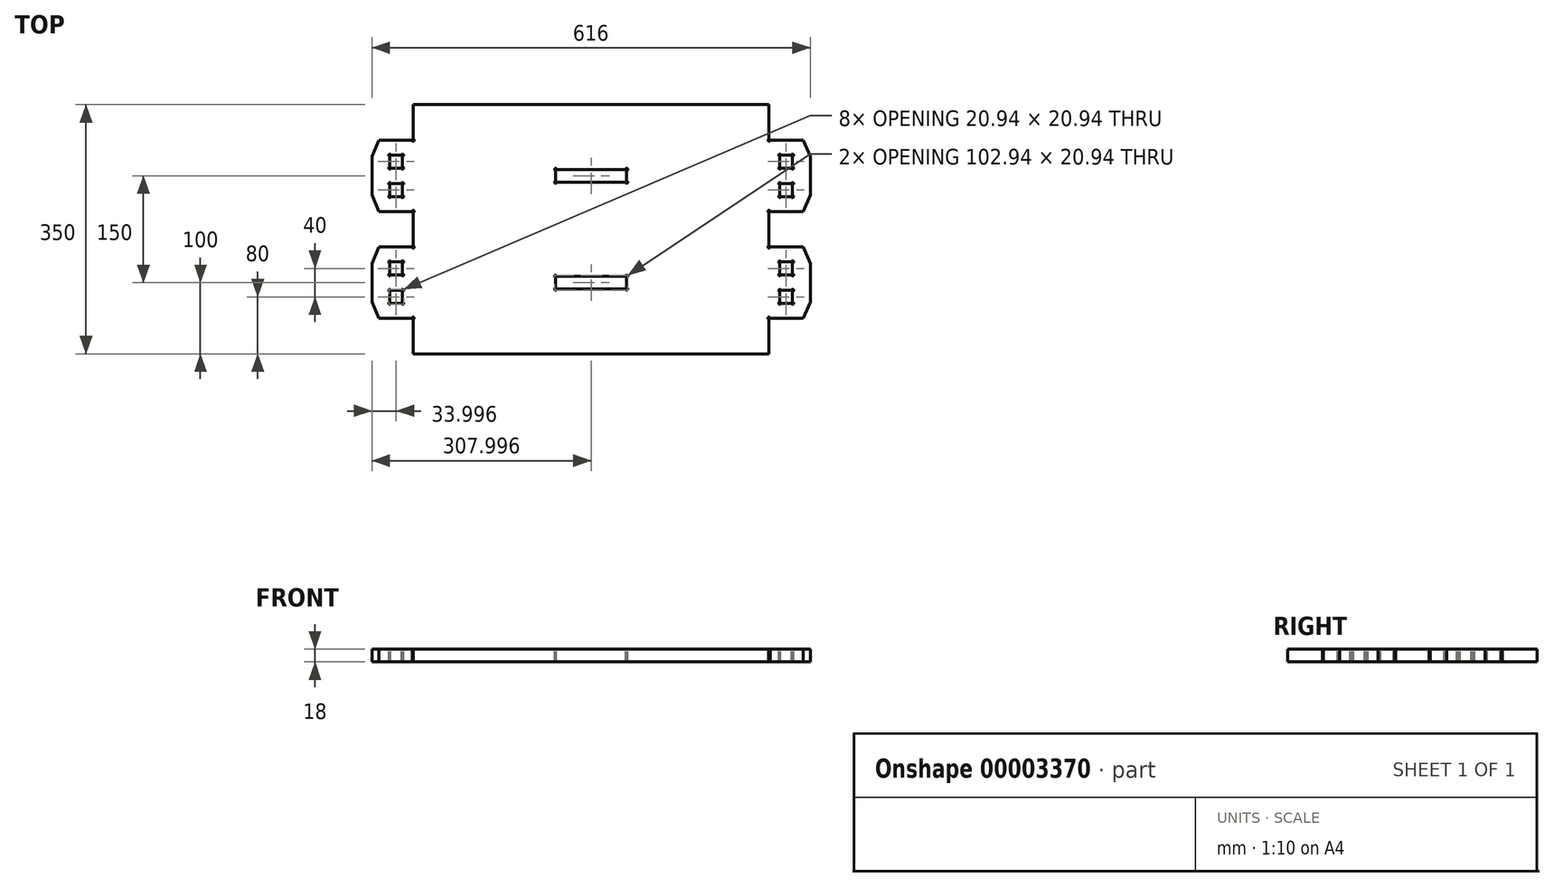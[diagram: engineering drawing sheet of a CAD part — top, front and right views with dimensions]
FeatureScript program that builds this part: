
annotation { "Feature Type Name" : "Feature", "Feature Type Description" : "" }
export const myFeature = defineFeature(function(context is Context, id is Id, definition is map)
    precondition{}
    {
        {
            var Q0;
            Q0=qCreatedBy(makeId("Top.planeOp"),FACE);
            var sketch = newSketch(context, id + "F0", { "sketchPlane" : qUnion([Q0])});
            skLineSegment(sketch, "E0.bottom", {"start": v(-333.81, 50) * mm, "end": v(166.19, 50) * mm});
            skLineSegment(sketch, "E0.top", {"start": v(-333.81, -300) * mm, "end": v(166.19, -300) * mm});
            skLineSegment(sketch, "E1.bottom", {"start": v(-333.81, -250) * mm, "end": v(-391.81, -250) * mm});
            skLineSegment(sketch, "E1.top", {"start": v(-333.81, -150) * mm, "end": v(-391.81, -150) * mm});
            skLineSegment(sketch, "E1.right", {"start": v(-391.81, -250) * mm, "end": v(-391.81, -150) * mm});
            skLineSegment(sketch, "E2.bottom", {"start": v(-333.81, -100) * mm, "end": v(-391.81, -100) * mm});
            skLineSegment(sketch, "E2.top", {"start": v(-333.81, 0) * mm, "end": v(-391.81, 0) * mm});
            skLineSegment(sketch, "E2.right", {"start": v(-391.81, -100) * mm, "end": v(-391.81, 0) * mm});
            skLineSegment(sketch, "E3.bottom", {"start": v(166.19, -250) * mm, "end": v(224.19, -250) * mm});
            skLineSegment(sketch, "E3.top", {"start": v(166.19, -150) * mm, "end": v(224.19, -150) * mm});
            skLineSegment(sketch, "E3.right", {"start": v(224.19, -250) * mm, "end": v(224.19, -150) * mm});
            skLineSegment(sketch, "E4.bottom", {"start": v(166.19, -100) * mm, "end": v(224.19, -100) * mm});
            skLineSegment(sketch, "E4.top", {"start": v(166.19, 0) * mm, "end": v(224.19, 0) * mm});
            skLineSegment(sketch, "E4.right", {"start": v(224.19, -100) * mm, "end": v(224.19, 0) * mm});
            skLineSegment(sketch, "E5", {"start": v(-333.81, -300) * mm, "end": v(-333.81, -250) * mm});
            skLineSegment(sketch, "E6", {"start": v(-333.81, -150) * mm, "end": v(-333.81, -100) * mm});
            skLineSegment(sketch, "E7", {"start": v(-333.81, 0) * mm, "end": v(-333.81, 50) * mm});
            skLineSegment(sketch, "E8", {"start": v(166.19, -300) * mm, "end": v(166.19, -250) * mm});
            skLineSegment(sketch, "E9", {"start": v(166.19, -150) * mm, "end": v(166.19, -100) * mm});
            skLineSegment(sketch, "E10", {"start": v(166.19, 0) * mm, "end": v(166.19, 50) * mm});
            skLineSegment(sketch, "E11", {"start": v(-366.81, -79) * mm, "end": v(-348.81, -79) * mm, "construction": true});
            skLineSegment(sketch, "E12", {"start": v(-366.81, -21) * mm, "end": v(-348.81, -21) * mm, "construction": true});
            skLineSegment(sketch, "E13.bottom", {"start": v(-348.81, -229) * mm, "end": v(-366.81, -229) * mm});
            skLineSegment(sketch, "E13.top", {"start": v(-348.81, -211) * mm, "end": v(-366.81, -211) * mm});
            skLineSegment(sketch, "E13.left", {"start": v(-348.81, -229) * mm, "end": v(-348.81, -211) * mm});
            skLineSegment(sketch, "E13.right", {"start": v(-366.81, -229) * mm, "end": v(-366.81, -211) * mm});
            skLineSegment(sketch, "E14.bottom", {"start": v(-348.81, -171) * mm, "end": v(-366.81, -171) * mm});
            skLineSegment(sketch, "E14.top", {"start": v(-348.81, -189) * mm, "end": v(-366.81, -189) * mm});
            skLineSegment(sketch, "E14.left", {"start": v(-348.81, -171) * mm, "end": v(-348.81, -189) * mm});
            skLineSegment(sketch, "E14.right", {"start": v(-366.81, -171) * mm, "end": v(-366.81, -189) * mm});
            skLineSegment(sketch, "E15.bottom", {"start": v(-348.81, -79) * mm, "end": v(-366.81, -79) * mm});
            skLineSegment(sketch, "E15.top", {"start": v(-348.81, -61) * mm, "end": v(-366.81, -61) * mm});
            skLineSegment(sketch, "E15.left", {"start": v(-348.81, -79) * mm, "end": v(-348.81, -61) * mm});
            skLineSegment(sketch, "E15.right", {"start": v(-366.81, -79) * mm, "end": v(-366.81, -61) * mm});
            skLineSegment(sketch, "E16.bottom", {"start": v(-348.81, -21) * mm, "end": v(-366.81, -21) * mm});
            skLineSegment(sketch, "E16.top", {"start": v(-348.81, -39) * mm, "end": v(-366.81, -39) * mm});
            skLineSegment(sketch, "E16.left", {"start": v(-348.81, -21) * mm, "end": v(-348.81, -39) * mm});
            skLineSegment(sketch, "E16.right", {"start": v(-366.81, -21) * mm, "end": v(-366.81, -39) * mm});
            skLineSegment(sketch, "E17.bottom", {"start": v(181.19, -229) * mm, "end": v(199.19, -229) * mm});
            skLineSegment(sketch, "E17.top", {"start": v(181.19, -211) * mm, "end": v(199.19, -211) * mm});
            skLineSegment(sketch, "E17.left", {"start": v(181.19, -229) * mm, "end": v(181.19, -211) * mm});
            skLineSegment(sketch, "E17.right", {"start": v(199.19, -229) * mm, "end": v(199.19, -211) * mm});
            skLineSegment(sketch, "E18.bottom", {"start": v(181.19, -171) * mm, "end": v(199.19, -171) * mm});
            skLineSegment(sketch, "E18.top", {"start": v(181.19, -189) * mm, "end": v(199.19, -189) * mm});
            skLineSegment(sketch, "E18.left", {"start": v(181.19, -171) * mm, "end": v(181.19, -189) * mm});
            skLineSegment(sketch, "E18.right", {"start": v(199.19, -171) * mm, "end": v(199.19, -189) * mm});
            skLineSegment(sketch, "E19.bottom", {"start": v(181.19, -79) * mm, "end": v(199.19, -79) * mm});
            skLineSegment(sketch, "E19.top", {"start": v(181.19, -61) * mm, "end": v(199.19, -61) * mm});
            skLineSegment(sketch, "E19.left", {"start": v(181.19, -79) * mm, "end": v(181.19, -61) * mm});
            skLineSegment(sketch, "E19.right", {"start": v(199.19, -79) * mm, "end": v(199.19, -61) * mm});
            skLineSegment(sketch, "E20.bottom", {"start": v(181.19, -21) * mm, "end": v(199.19, -21) * mm});
            skLineSegment(sketch, "E20.top", {"start": v(181.19, -39) * mm, "end": v(199.19, -39) * mm});
            skLineSegment(sketch, "E20.left", {"start": v(181.19, -21) * mm, "end": v(181.19, -39) * mm});
            skLineSegment(sketch, "E20.right", {"start": v(199.19, -21) * mm, "end": v(199.19, -39) * mm});
            skLineSegment(sketch, "E21.bottom", {"start": v(-133.81, -209) * mm, "end": v(-33.81, -209) * mm});
            skLineSegment(sketch, "E21.top", {"start": v(-133.81, -191) * mm, "end": v(-33.81, -191) * mm});
            skLineSegment(sketch, "E21.left", {"start": v(-133.81, -209) * mm, "end": v(-133.81, -191) * mm});
            skLineSegment(sketch, "E21.right", {"start": v(-33.81, -209) * mm, "end": v(-33.81, -191) * mm});
            skLineSegment(sketch, "E22.bottom", {"start": v(-133.81, -59) * mm, "end": v(-33.81, -59) * mm});
            skLineSegment(sketch, "E22.top", {"start": v(-133.81, -41) * mm, "end": v(-33.81, -41) * mm});
            skLineSegment(sketch, "E22.left", {"start": v(-133.81, -59) * mm, "end": v(-133.81, -41) * mm});
            skLineSegment(sketch, "E22.right", {"start": v(-33.81, -59) * mm, "end": v(-33.81, -41) * mm});
            skSolve(sketch);
        }
        {
            var Q0;
            Q0=makeQuery(id+"F0.imprint","IMPRINT",FACE,{"disambiguationData":[TD([[makeQuery(id+"F0.imprint","IMPRINT",EDGE,{"derivedFrom":sQuery(id+"F0.wireOp",EDGE,"E0.bottom")}),-1.0]])]});
            extrude(context, id + "F1", {"entities" : qUnion([Q0]), "depth" : 18 * mm});
        }
        {
            var Q0;
            Q0=makeQuery(id+"F1.opExtrude","SWEPT_EDGE",EDGE,{"disambiguationData":[OSD([sQuery(id+"F0.wireOp",EDGE,"E1.bottom"),sQuery(id+"F0.wireOp",EDGE,"E1.right")])]});
            var Q1;
            Q1=makeQuery(id+"F1.opExtrude","SWEPT_EDGE",EDGE,{"disambiguationData":[OSD([sQuery(id+"F0.wireOp",EDGE,"E1.top"),sQuery(id+"F0.wireOp",EDGE,"E1.right")])]});
            var Q2;
            Q2=makeQuery(id+"F1.opExtrude","SWEPT_EDGE",EDGE,{"disambiguationData":[OSD([sQuery(id+"F0.wireOp",EDGE,"E2.bottom"),sQuery(id+"F0.wireOp",EDGE,"E2.right")])]});
            var Q3;
            Q3=makeQuery(id+"F1.opExtrude","SWEPT_EDGE",EDGE,{"disambiguationData":[OSD([sQuery(id+"F0.wireOp",EDGE,"E3.top"),sQuery(id+"F0.wireOp",EDGE,"E3.right")])]});
            var Q4;
            Q4=makeQuery(id+"F1.opExtrude","SWEPT_EDGE",EDGE,{"disambiguationData":[OSD([sQuery(id+"F0.wireOp",EDGE,"E4.top"),sQuery(id+"F0.wireOp",EDGE,"E4.right")])]});
            chamfer(context, id + "F2", {"entities" : qUnion([Q0, Q1, Q2, Q3, Q4]), "chamferType" : ChamferType.TWO_OFFSETS, "width1" : 10 * mm, "oppositeDirection" : false, "width2" : 23 * mm, "tangentPropagation" : true});
        }
        {
            var Q0;
            Q0=makeQuery(id+"F1.opExtrude","SWEPT_EDGE",EDGE,{"disambiguationData":[OSD([sQuery(id+"F0.wireOp",EDGE,"E2.top"),sQuery(id+"F0.wireOp",EDGE,"E2.right")])]});
            var Q1;
            Q1=makeQuery(id+"F1.opExtrude","SWEPT_EDGE",EDGE,{"disambiguationData":[OSD([sQuery(id+"F0.wireOp",EDGE,"E4.bottom"),sQuery(id+"F0.wireOp",EDGE,"E4.right")])]});
            var Q2;
            Q2=makeQuery(id+"F1.opExtrude","SWEPT_EDGE",EDGE,{"disambiguationData":[OSD([sQuery(id+"F0.wireOp",EDGE,"E3.bottom"),sQuery(id+"F0.wireOp",EDGE,"E3.right")])]});
            chamfer(context, id + "F3", {"entities" : qUnion([Q0, Q1, Q2]), "chamferType" : ChamferType.TWO_OFFSETS, "width1" : 23 * mm, "oppositeDirection" : false, "width2" : 10 * mm, "tangentPropagation" : true});
        }
        {
            var Q0;
            Q0=makeQuery(id+"F1.opExtrude","CAP_FACE",FACE,{"disambiguationData":[OSD([sQuery(id+"F0.wireOp",EDGE,"E0.bottom"),sQuery(id+"F0.wireOp",EDGE,"E0.top"),sQuery(id+"F0.wireOp",EDGE,"E1.bottom"),sQuery(id+"F0.wireOp",EDGE,"E1.top"),sQuery(id+"F0.wireOp",EDGE,"E1.right"),sQuery(id+"F0.wireOp",EDGE,"E2.bottom"),sQuery(id+"F0.wireOp",EDGE,"E2.top"),sQuery(id+"F0.wireOp",EDGE,"E2.right"),sQuery(id+"F0.wireOp",EDGE,"E3.bottom"),sQuery(id+"F0.wireOp",EDGE,"E3.top"),sQuery(id+"F0.wireOp",EDGE,"E3.right"),sQuery(id+"F0.wireOp",EDGE,"E4.bottom"),sQuery(id+"F0.wireOp",EDGE,"E4.top"),sQuery(id+"F0.wireOp",EDGE,"E4.right"),sQuery(id+"F0.wireOp",EDGE,"E5"),sQuery(id+"F0.wireOp",EDGE,"E6"),sQuery(id+"F0.wireOp",EDGE,"E7"),sQuery(id+"F0.wireOp",EDGE,"E8"),sQuery(id+"F0.wireOp",EDGE,"E9"),sQuery(id+"F0.wireOp",EDGE,"E10"),sQuery(id+"F0.wireOp",EDGE,"E13.bottom"),sQuery(id+"F0.wireOp",EDGE,"E13.top"),sQuery(id+"F0.wireOp",EDGE,"E13.left"),sQuery(id+"F0.wireOp",EDGE,"E13.right"),sQuery(id+"F0.wireOp",EDGE,"E14.bottom"),sQuery(id+"F0.wireOp",EDGE,"E14.top"),sQuery(id+"F0.wireOp",EDGE,"E14.left"),sQuery(id+"F0.wireOp",EDGE,"E14.right"),sQuery(id+"F0.wireOp",EDGE,"E15.bottom"),sQuery(id+"F0.wireOp",EDGE,"E15.top"),sQuery(id+"F0.wireOp",EDGE,"E15.left"),sQuery(id+"F0.wireOp",EDGE,"E15.right"),sQuery(id+"F0.wireOp",EDGE,"E16.bottom"),sQuery(id+"F0.wireOp",EDGE,"E16.top"),sQuery(id+"F0.wireOp",EDGE,"E16.left"),sQuery(id+"F0.wireOp",EDGE,"E16.right"),sQuery(id+"F0.wireOp",EDGE,"E17.bottom"),sQuery(id+"F0.wireOp",EDGE,"E17.top"),sQuery(id+"F0.wireOp",EDGE,"E17.left"),sQuery(id+"F0.wireOp",EDGE,"E17.right"),sQuery(id+"F0.wireOp",EDGE,"E18.bottom"),sQuery(id+"F0.wireOp",EDGE,"E18.top"),sQuery(id+"F0.wireOp",EDGE,"E18.left"),sQuery(id+"F0.wireOp",EDGE,"E18.right"),sQuery(id+"F0.wireOp",EDGE,"E19.bottom"),sQuery(id+"F0.wireOp",EDGE,"E19.top"),sQuery(id+"F0.wireOp",EDGE,"E19.left"),sQuery(id+"F0.wireOp",EDGE,"E19.right"),sQuery(id+"F0.wireOp",EDGE,"E20.bottom"),sQuery(id+"F0.wireOp",EDGE,"E20.top"),sQuery(id+"F0.wireOp",EDGE,"E20.left"),sQuery(id+"F0.wireOp",EDGE,"E20.right"),sQuery(id+"F0.wireOp",EDGE,"E21.bottom"),sQuery(id+"F0.wireOp",EDGE,"E21.top"),sQuery(id+"F0.wireOp",EDGE,"E21.left"),sQuery(id+"F0.wireOp",EDGE,"E21.right"),sQuery(id+"F0.wireOp",EDGE,"E22.bottom"),sQuery(id+"F0.wireOp",EDGE,"E22.top"),sQuery(id+"F0.wireOp",EDGE,"E22.left"),sQuery(id+"F0.wireOp",EDGE,"E22.right")])],"isStart":false});
            var sketch = newSketch(context, id + "F4", { "sketchPlane" : qUnion([Q0])});
            skCircle(sketch, "E23", {"center": v(-348.81, -211) * mm, "radius": 1.5 * mm});
            skCircle(sketch, "E24", {"center": v(-348.81, -229) * mm, "radius": 1.5 * mm});
            skCircle(sketch, "E25", {"center": v(-366.81, -229) * mm, "radius": 1.5 * mm});
            skCircle(sketch, "E26", {"center": v(-366.81, -211) * mm, "radius": 1.5 * mm});
            skCircle(sketch, "E27", {"center": v(-366.81, -189) * mm, "radius": 1.5 * mm});
            skCircle(sketch, "E28", {"center": v(-366.81, -171) * mm, "radius": 1.5 * mm});
            skCircle(sketch, "E29", {"center": v(-348.81, -171) * mm, "radius": 1.5 * mm});
            skCircle(sketch, "E30", {"center": v(-348.81, -189) * mm, "radius": 1.5 * mm});
            skCircle(sketch, "E31", {"center": v(-348.81, -79) * mm, "radius": 1.5 * mm});
            skCircle(sketch, "E32", {"center": v(-348.81, -61) * mm, "radius": 1.5 * mm});
            skCircle(sketch, "E33", {"center": v(-366.81, -79) * mm, "radius": 1.5 * mm});
            skCircle(sketch, "E34", {"center": v(-366.81, -61) * mm, "radius": 1.5 * mm});
            skCircle(sketch, "E35", {"center": v(-348.81, -39) * mm, "radius": 1.5 * mm});
            skCircle(sketch, "E36", {"center": v(-348.81, -21) * mm, "radius": 1.5 * mm});
            skCircle(sketch, "E37", {"center": v(-366.81, -39) * mm, "radius": 1.5 * mm});
            skCircle(sketch, "E38", {"center": v(-366.81, -21) * mm, "radius": 1.5 * mm});
            skCircle(sketch, "E39", {"center": v(-133.81, -209) * mm, "radius": 1.5 * mm});
            skCircle(sketch, "E40", {"center": v(-133.81, -191) * mm, "radius": 1.5 * mm});
            skCircle(sketch, "E41", {"center": v(-33.81, -191) * mm, "radius": 1.5 * mm});
            skCircle(sketch, "E42", {"center": v(-33.81, -209) * mm, "radius": 1.5 * mm});
            skCircle(sketch, "E43", {"center": v(-133.81, -59) * mm, "radius": 1.5 * mm});
            skCircle(sketch, "E44", {"center": v(-133.81, -41) * mm, "radius": 1.5 * mm});
            skCircle(sketch, "E45", {"center": v(-33.81, -41) * mm, "radius": 1.5 * mm});
            skCircle(sketch, "E46", {"center": v(-33.81, -59) * mm, "radius": 1.5 * mm});
            skCircle(sketch, "E47", {"center": v(181.19, -229) * mm, "radius": 1.5 * mm});
            skCircle(sketch, "E48", {"center": v(181.19, -211) * mm, "radius": 1.5 * mm});
            skCircle(sketch, "E49", {"center": v(199.19, -211) * mm, "radius": 1.5 * mm});
            skCircle(sketch, "E50", {"center": v(199.19, -229) * mm, "radius": 1.5 * mm});
            skCircle(sketch, "E51", {"center": v(199.19, -171) * mm, "radius": 1.5 * mm});
            skCircle(sketch, "E52", {"center": v(181.19, -171) * mm, "radius": 1.5 * mm});
            skCircle(sketch, "E53", {"center": v(181.19, -189) * mm, "radius": 1.5 * mm});
            skCircle(sketch, "E54", {"center": v(181.19, -79) * mm, "radius": 1.5 * mm});
            skCircle(sketch, "E55", {"center": v(181.19, -61) * mm, "radius": 1.5 * mm});
            skCircle(sketch, "E56", {"center": v(199.19, -61) * mm, "radius": 1.5 * mm});
            skCircle(sketch, "E57", {"center": v(199.19, -79) * mm, "radius": 1.5 * mm});
            skCircle(sketch, "E58", {"center": v(199.19, -39) * mm, "radius": 1.5 * mm});
            skCircle(sketch, "E59", {"center": v(181.19, -39) * mm, "radius": 1.5 * mm});
            skCircle(sketch, "E60", {"center": v(181.19, -21) * mm, "radius": 1.5 * mm});
            skCircle(sketch, "E61", {"center": v(199.19, -21) * mm, "radius": 1.5 * mm});
            skCircle(sketch, "E62", {"center": v(166.19, -100) * mm, "radius": 1.5 * mm});
            skCircle(sketch, "E63", {"center": v(166.19, -150) * mm, "radius": 1.5 * mm});
            skCircle(sketch, "E64", {"center": v(166.19, -250) * mm, "radius": 1.5 * mm});
            skCircle(sketch, "E65", {"center": v(166.19, 0) * mm, "radius": 1.5 * mm});
            skCircle(sketch, "E66", {"center": v(-333.81, -250) * mm, "radius": 1.5 * mm});
            skCircle(sketch, "E67", {"center": v(-333.81, -150) * mm, "radius": 1.5 * mm});
            skCircle(sketch, "E68", {"center": v(-333.81, -100) * mm, "radius": 1.5 * mm});
            skCircle(sketch, "E69", {"center": v(-333.81, 0) * mm, "radius": 1.5 * mm});
            skCircle(sketch, "E70", {"center": v(199.19, -189) * mm, "radius": 1.5 * mm});
            skSolve(sketch);
        }
        {
            var Q0;
            {var subQ1=sQuery(id+"F4.wireOp",EDGE,"E62");var subQ3=makeQuery(id+"F1.opExtrude","CAP_EDGE",EDGE,{"disambiguationData":[OSD([sQuery(id+"F0.wireOp",EDGE,"E9")])],"isStart":false});var subQ6=makeQuery(id+"F4.imprint","INTERSECT",VERTEX,{"derivedFrom":[subQ3,subQ1]});var subQ9=sQuery(id+"F4.wireOp",EDGE,"E63");var subQ13=makeQuery(id+"F4.imprint","INTERSECT",VERTEX,{"derivedFrom":[subQ3,subQ9]});var subQ16=sQuery(id+"F4.wireOp",EDGE,"E64");var subQ18=makeQuery(id+"F1.opExtrude","CAP_EDGE",EDGE,{"disambiguationData":[OSD([sQuery(id+"F0.wireOp",EDGE,"E8")])],"isStart":false});var subQ21=makeQuery(id+"F4.imprint","INTERSECT",VERTEX,{"derivedFrom":[subQ18,subQ16]});var subQ24=sQuery(id+"F4.wireOp",EDGE,"E65");var subQ26=makeQuery(id+"F1.opExtrude","CAP_EDGE",EDGE,{"disambiguationData":[OSD([sQuery(id+"F0.wireOp",EDGE,"E10")])],"isStart":false});var subQ29=makeQuery(id+"F4.imprint","INTERSECT",VERTEX,{"derivedFrom":[subQ26,subQ24]});var subQ32=sQuery(id+"F4.wireOp",EDGE,"E66");var subQ34=makeQuery(id+"F1.opExtrude","CAP_EDGE",EDGE,{"disambiguationData":[OSD([sQuery(id+"F0.wireOp",EDGE,"E5")])],"isStart":false});var subQ37=makeQuery(id+"F4.imprint","INTERSECT",VERTEX,{"derivedFrom":[subQ34,subQ32]});var subQ40=sQuery(id+"F4.wireOp",EDGE,"E67");var subQ42=makeQuery(id+"F1.opExtrude","CAP_EDGE",EDGE,{"disambiguationData":[OSD([sQuery(id+"F0.wireOp",EDGE,"E6")])],"isStart":false});var subQ45=makeQuery(id+"F4.imprint","INTERSECT",VERTEX,{"derivedFrom":[subQ42,subQ40]});var subQ48=sQuery(id+"F4.wireOp",EDGE,"E68");var subQ52=makeQuery(id+"F4.imprint","INTERSECT",VERTEX,{"derivedFrom":[subQ42,subQ48]});var subQ55=sQuery(id+"F4.wireOp",EDGE,"E69");var subQ57=makeQuery(id+"F1.opExtrude","CAP_EDGE",EDGE,{"disambiguationData":[OSD([sQuery(id+"F0.wireOp",EDGE,"E7")])],"isStart":false});var subQ60=makeQuery(id+"F4.imprint","INTERSECT",VERTEX,{"derivedFrom":[subQ57,subQ55]});var subQ63=sQuery(id+"F4.wireOp",EDGE,"E23");var subQ65=makeQuery(id+"F1.opExtrude","CAP_EDGE",EDGE,{"disambiguationData":[OSD([sQuery(id+"F0.wireOp",EDGE,"E13.top")])],"isStart":false});var subQ68=makeQuery(id+"F4.imprint","INTERSECT",VERTEX,{"derivedFrom":[subQ65,subQ63]});var subQ70=sQuery(id+"F4.wireOp",EDGE,"E24");var subQ72=makeQuery(id+"F1.opExtrude","CAP_EDGE",EDGE,{"disambiguationData":[OSD([sQuery(id+"F0.wireOp",EDGE,"E13.bottom")])],"isStart":false});var subQ75=makeQuery(id+"F4.imprint","INTERSECT",VERTEX,{"derivedFrom":[subQ72,subQ70]});var subQ78=sQuery(id+"F4.wireOp",EDGE,"E25");var subQ82=makeQuery(id+"F4.imprint","INTERSECT",VERTEX,{"derivedFrom":[subQ72,subQ78]});var subQ84=sQuery(id+"F4.wireOp",EDGE,"E26");var subQ88=makeQuery(id+"F4.imprint","INTERSECT",VERTEX,{"derivedFrom":[subQ65,subQ84]});var subQ91=sQuery(id+"F4.wireOp",EDGE,"E27");var subQ93=makeQuery(id+"F1.opExtrude","CAP_EDGE",EDGE,{"disambiguationData":[OSD([sQuery(id+"F0.wireOp",EDGE,"E14.top")])],"isStart":false});var subQ96=makeQuery(id+"F4.imprint","INTERSECT",VERTEX,{"derivedFrom":[subQ93,subQ91]});var subQ98=sQuery(id+"F4.wireOp",EDGE,"E28");var subQ100=makeQuery(id+"F1.opExtrude","CAP_EDGE",EDGE,{"disambiguationData":[OSD([sQuery(id+"F0.wireOp",EDGE,"E14.bottom")])],"isStart":false});var subQ103=makeQuery(id+"F4.imprint","INTERSECT",VERTEX,{"derivedFrom":[subQ100,subQ98]});var subQ106=sQuery(id+"F4.wireOp",EDGE,"E29");var subQ110=makeQuery(id+"F4.imprint","INTERSECT",VERTEX,{"derivedFrom":[subQ100,subQ106]});var subQ112=sQuery(id+"F4.wireOp",EDGE,"E30");var subQ116=makeQuery(id+"F4.imprint","INTERSECT",VERTEX,{"derivedFrom":[subQ93,subQ112]});var subQ119=sQuery(id+"F4.wireOp",EDGE,"E31");var subQ121=makeQuery(id+"F1.opExtrude","CAP_EDGE",EDGE,{"disambiguationData":[OSD([sQuery(id+"F0.wireOp",EDGE,"E15.bottom")])],"isStart":false});var subQ124=makeQuery(id+"F4.imprint","INTERSECT",VERTEX,{"derivedFrom":[subQ121,subQ119]});var subQ126=sQuery(id+"F4.wireOp",EDGE,"E32");var subQ128=makeQuery(id+"F1.opExtrude","CAP_EDGE",EDGE,{"disambiguationData":[OSD([sQuery(id+"F0.wireOp",EDGE,"E15.top")])],"isStart":false});var subQ131=makeQuery(id+"F4.imprint","INTERSECT",VERTEX,{"derivedFrom":[subQ128,subQ126]});var subQ134=sQuery(id+"F4.wireOp",EDGE,"E33");var subQ138=makeQuery(id+"F4.imprint","INTERSECT",VERTEX,{"derivedFrom":[subQ121,subQ134]});var subQ140=sQuery(id+"F4.wireOp",EDGE,"E34");var subQ144=makeQuery(id+"F4.imprint","INTERSECT",VERTEX,{"derivedFrom":[subQ128,subQ140]});var subQ147=sQuery(id+"F4.wireOp",EDGE,"E35");var subQ149=makeQuery(id+"F1.opExtrude","CAP_EDGE",EDGE,{"disambiguationData":[OSD([sQuery(id+"F0.wireOp",EDGE,"E16.top")])],"isStart":false});var subQ152=makeQuery(id+"F4.imprint","INTERSECT",VERTEX,{"derivedFrom":[subQ149,subQ147]});var subQ154=sQuery(id+"F4.wireOp",EDGE,"E36");var subQ156=makeQuery(id+"F1.opExtrude","CAP_EDGE",EDGE,{"disambiguationData":[OSD([sQuery(id+"F0.wireOp",EDGE,"E16.bottom")])],"isStart":false});var subQ159=makeQuery(id+"F4.imprint","INTERSECT",VERTEX,{"derivedFrom":[subQ156,subQ154]});var subQ162=sQuery(id+"F4.wireOp",EDGE,"E37");var subQ166=makeQuery(id+"F4.imprint","INTERSECT",VERTEX,{"derivedFrom":[subQ149,subQ162]});var subQ168=sQuery(id+"F4.wireOp",EDGE,"E38");var subQ172=makeQuery(id+"F4.imprint","INTERSECT",VERTEX,{"derivedFrom":[subQ156,subQ168]});var subQ175=sQuery(id+"F4.wireOp",EDGE,"E39");var subQ177=makeQuery(id+"F1.opExtrude","CAP_EDGE",EDGE,{"disambiguationData":[OSD([sQuery(id+"F0.wireOp",EDGE,"E21.bottom")])],"isStart":false});var subQ180=makeQuery(id+"F4.imprint","INTERSECT",VERTEX,{"derivedFrom":[subQ177,subQ175]});var subQ182=sQuery(id+"F4.wireOp",EDGE,"E40");var subQ184=makeQuery(id+"F1.opExtrude","CAP_EDGE",EDGE,{"disambiguationData":[OSD([sQuery(id+"F0.wireOp",EDGE,"E21.top")])],"isStart":false});var subQ187=makeQuery(id+"F4.imprint","INTERSECT",VERTEX,{"derivedFrom":[subQ184,subQ182]});var subQ190=sQuery(id+"F4.wireOp",EDGE,"E41");var subQ194=makeQuery(id+"F4.imprint","INTERSECT",VERTEX,{"derivedFrom":[subQ184,subQ190]});var subQ196=sQuery(id+"F4.wireOp",EDGE,"E42");var subQ200=makeQuery(id+"F4.imprint","INTERSECT",VERTEX,{"derivedFrom":[subQ177,subQ196]});var subQ203=sQuery(id+"F4.wireOp",EDGE,"E43");var subQ205=makeQuery(id+"F1.opExtrude","CAP_EDGE",EDGE,{"disambiguationData":[OSD([sQuery(id+"F0.wireOp",EDGE,"E22.bottom")])],"isStart":false});var subQ208=makeQuery(id+"F4.imprint","INTERSECT",VERTEX,{"derivedFrom":[subQ205,subQ203]});var subQ210=sQuery(id+"F4.wireOp",EDGE,"E44");var subQ212=makeQuery(id+"F1.opExtrude","CAP_EDGE",EDGE,{"disambiguationData":[OSD([sQuery(id+"F0.wireOp",EDGE,"E22.top")])],"isStart":false});var subQ215=makeQuery(id+"F4.imprint","INTERSECT",VERTEX,{"derivedFrom":[subQ212,subQ210]});var subQ218=sQuery(id+"F4.wireOp",EDGE,"E45");var subQ222=makeQuery(id+"F4.imprint","INTERSECT",VERTEX,{"derivedFrom":[subQ212,subQ218]});var subQ224=sQuery(id+"F4.wireOp",EDGE,"E46");var subQ228=makeQuery(id+"F4.imprint","INTERSECT",VERTEX,{"derivedFrom":[subQ205,subQ224]});var subQ231=sQuery(id+"F4.wireOp",EDGE,"E47");var subQ233=makeQuery(id+"F1.opExtrude","CAP_EDGE",EDGE,{"disambiguationData":[OSD([sQuery(id+"F0.wireOp",EDGE,"E17.bottom")])],"isStart":false});var subQ236=makeQuery(id+"F4.imprint","INTERSECT",VERTEX,{"derivedFrom":[subQ233,subQ231]});var subQ238=sQuery(id+"F4.wireOp",EDGE,"E48");var subQ240=makeQuery(id+"F1.opExtrude","CAP_EDGE",EDGE,{"disambiguationData":[OSD([sQuery(id+"F0.wireOp",EDGE,"E17.top")])],"isStart":false});var subQ243=makeQuery(id+"F4.imprint","INTERSECT",VERTEX,{"derivedFrom":[subQ240,subQ238]});var subQ246=sQuery(id+"F4.wireOp",EDGE,"E49");var subQ250=makeQuery(id+"F4.imprint","INTERSECT",VERTEX,{"derivedFrom":[subQ240,subQ246]});var subQ252=sQuery(id+"F4.wireOp",EDGE,"E50");var subQ256=makeQuery(id+"F4.imprint","INTERSECT",VERTEX,{"derivedFrom":[subQ233,subQ252]});var subQ259=sQuery(id+"F4.wireOp",EDGE,"E51");var subQ261=makeQuery(id+"F1.opExtrude","CAP_EDGE",EDGE,{"disambiguationData":[OSD([sQuery(id+"F0.wireOp",EDGE,"E18.bottom")])],"isStart":false});var subQ264=makeQuery(id+"F4.imprint","INTERSECT",VERTEX,{"derivedFrom":[subQ261,subQ259]});var subQ267=sQuery(id+"F4.wireOp",EDGE,"E52");var subQ271=makeQuery(id+"F4.imprint","INTERSECT",VERTEX,{"derivedFrom":[subQ261,subQ267]});var subQ273=sQuery(id+"F4.wireOp",EDGE,"E53");var subQ275=makeQuery(id+"F1.opExtrude","CAP_EDGE",EDGE,{"disambiguationData":[OSD([sQuery(id+"F0.wireOp",EDGE,"E18.top")])],"isStart":false});var subQ278=makeQuery(id+"F4.imprint","INTERSECT",VERTEX,{"derivedFrom":[subQ275,subQ273]});var subQ281=sQuery(id+"F4.wireOp",EDGE,"E54");var subQ283=makeQuery(id+"F1.opExtrude","CAP_EDGE",EDGE,{"disambiguationData":[OSD([sQuery(id+"F0.wireOp",EDGE,"E19.bottom")])],"isStart":false});var subQ286=makeQuery(id+"F4.imprint","INTERSECT",VERTEX,{"derivedFrom":[subQ283,subQ281]});var subQ288=sQuery(id+"F4.wireOp",EDGE,"E55");var subQ290=makeQuery(id+"F1.opExtrude","CAP_EDGE",EDGE,{"disambiguationData":[OSD([sQuery(id+"F0.wireOp",EDGE,"E19.top")])],"isStart":false});var subQ293=makeQuery(id+"F4.imprint","INTERSECT",VERTEX,{"derivedFrom":[subQ290,subQ288]});var subQ296=sQuery(id+"F4.wireOp",EDGE,"E56");var subQ300=makeQuery(id+"F4.imprint","INTERSECT",VERTEX,{"derivedFrom":[subQ290,subQ296]});var subQ302=sQuery(id+"F4.wireOp",EDGE,"E57");var subQ306=makeQuery(id+"F4.imprint","INTERSECT",VERTEX,{"derivedFrom":[subQ283,subQ302]});var subQ309=sQuery(id+"F4.wireOp",EDGE,"E58");var subQ311=makeQuery(id+"F1.opExtrude","CAP_EDGE",EDGE,{"disambiguationData":[OSD([sQuery(id+"F0.wireOp",EDGE,"E20.top")])],"isStart":false});var subQ314=makeQuery(id+"F4.imprint","INTERSECT",VERTEX,{"derivedFrom":[subQ311,subQ309]});var subQ317=sQuery(id+"F4.wireOp",EDGE,"E59");var subQ321=makeQuery(id+"F4.imprint","INTERSECT",VERTEX,{"derivedFrom":[subQ311,subQ317]});var subQ323=sQuery(id+"F4.wireOp",EDGE,"E60");var subQ325=makeQuery(id+"F1.opExtrude","CAP_EDGE",EDGE,{"disambiguationData":[OSD([sQuery(id+"F0.wireOp",EDGE,"E20.bottom")])],"isStart":false});var subQ328=makeQuery(id+"F4.imprint","INTERSECT",VERTEX,{"derivedFrom":[subQ325,subQ323]});var subQ330=sQuery(id+"F4.wireOp",EDGE,"E61");var subQ334=makeQuery(id+"F4.imprint","INTERSECT",VERTEX,{"derivedFrom":[subQ325,subQ330]});var subQ336=sQuery(id+"F4.wireOp",EDGE,"E70");var subQ340=makeQuery(id+"F4.imprint","INTERSECT",VERTEX,{"derivedFrom":[subQ275,subQ336]});Q0=qUnion([makeQuery(id+"F4.imprint","IMPRINT",FACE,{"disambiguationData":[TD([[makeQuery(id+"F4.imprint","IMPRINT",EDGE,{"disambiguationData":[TD([[subQ6,-1.0]])],"derivedFrom":subQ1}),1.0]])]}),makeQuery(id+"F4.imprint","IMPRINT",FACE,{"disambiguationData":[TD([[makeQuery(id+"F4.imprint","IMPRINT",EDGE,{"disambiguationData":[TD([[subQ13,1.0]])],"derivedFrom":subQ9}),1.0]])]}),makeQuery(id+"F4.imprint","IMPRINT",FACE,{"disambiguationData":[TD([[makeQuery(id+"F4.imprint","IMPRINT",EDGE,{"disambiguationData":[TD([[subQ21,-1.0]])],"derivedFrom":subQ16}),1.0]])]}),makeQuery(id+"F4.imprint","IMPRINT",FACE,{"disambiguationData":[TD([[makeQuery(id+"F4.imprint","IMPRINT",EDGE,{"disambiguationData":[TD([[subQ29,1.0]])],"derivedFrom":subQ24}),1.0]])]}),makeQuery(id+"F4.imprint","IMPRINT",FACE,{"disambiguationData":[TD([[makeQuery(id+"F4.imprint","IMPRINT",EDGE,{"disambiguationData":[TD([[subQ37,1.0]])],"derivedFrom":subQ32}),1.0]])]}),makeQuery(id+"F4.imprint","IMPRINT",FACE,{"disambiguationData":[TD([[makeQuery(id+"F4.imprint","IMPRINT",EDGE,{"disambiguationData":[TD([[subQ45,-1.0]])],"derivedFrom":subQ40}),1.0]])]}),makeQuery(id+"F4.imprint","IMPRINT",FACE,{"disambiguationData":[TD([[makeQuery(id+"F4.imprint","IMPRINT",EDGE,{"disambiguationData":[TD([[subQ52,1.0]])],"derivedFrom":subQ48}),1.0]])]}),makeQuery(id+"F4.imprint","IMPRINT",FACE,{"disambiguationData":[TD([[makeQuery(id+"F4.imprint","IMPRINT",EDGE,{"disambiguationData":[TD([[subQ60,-1.0]])],"derivedFrom":subQ55}),1.0]])]}),makeQuery(id+"F4.imprint","IMPRINT",FACE,{"disambiguationData":[TD([[makeQuery(id+"F4.imprint","IMPRINT",EDGE,{"disambiguationData":[TD([[subQ68,-1.0]])],"derivedFrom":subQ63}),1.0]])]}),makeQuery(id+"F4.imprint","IMPRINT",FACE,{"disambiguationData":[TD([[makeQuery(id+"F4.imprint","IMPRINT",EDGE,{"disambiguationData":[TD([[subQ68,1.0]])],"derivedFrom":subQ63}),1.0]])]}),makeQuery(id+"F4.imprint","IMPRINT",FACE,{"disambiguationData":[TD([[makeQuery(id+"F4.imprint","IMPRINT",EDGE,{"disambiguationData":[TD([[subQ75,1.0]])],"derivedFrom":subQ70}),1.0]])]}),makeQuery(id+"F4.imprint","IMPRINT",FACE,{"disambiguationData":[TD([[makeQuery(id+"F4.imprint","IMPRINT",EDGE,{"disambiguationData":[TD([[subQ75,-1.0]])],"derivedFrom":subQ70}),1.0]])]}),makeQuery(id+"F4.imprint","IMPRINT",FACE,{"disambiguationData":[TD([[makeQuery(id+"F4.imprint","IMPRINT",EDGE,{"disambiguationData":[TD([[subQ82,-1.0]])],"derivedFrom":subQ78}),1.0]])]}),makeQuery(id+"F4.imprint","IMPRINT",FACE,{"disambiguationData":[TD([[makeQuery(id+"F4.imprint","IMPRINT",EDGE,{"disambiguationData":[TD([[subQ82,1.0]])],"derivedFrom":subQ78}),1.0]])]}),makeQuery(id+"F4.imprint","IMPRINT",FACE,{"disambiguationData":[TD([[makeQuery(id+"F4.imprint","IMPRINT",EDGE,{"disambiguationData":[TD([[subQ88,-1.0]])],"derivedFrom":subQ84}),1.0]])]}),makeQuery(id+"F4.imprint","IMPRINT",FACE,{"disambiguationData":[TD([[makeQuery(id+"F4.imprint","IMPRINT",EDGE,{"disambiguationData":[TD([[subQ88,1.0]])],"derivedFrom":subQ84}),1.0]])]}),makeQuery(id+"F4.imprint","IMPRINT",FACE,{"disambiguationData":[TD([[makeQuery(id+"F4.imprint","IMPRINT",EDGE,{"disambiguationData":[TD([[subQ96,-1.0]])],"derivedFrom":subQ91}),1.0]])]}),makeQuery(id+"F4.imprint","IMPRINT",FACE,{"disambiguationData":[TD([[makeQuery(id+"F4.imprint","IMPRINT",EDGE,{"disambiguationData":[TD([[subQ96,1.0]])],"derivedFrom":subQ91}),1.0]])]}),makeQuery(id+"F4.imprint","IMPRINT",FACE,{"disambiguationData":[TD([[makeQuery(id+"F4.imprint","IMPRINT",EDGE,{"disambiguationData":[TD([[subQ103,-1.0]])],"derivedFrom":subQ98}),1.0]])]}),makeQuery(id+"F4.imprint","IMPRINT",FACE,{"disambiguationData":[TD([[makeQuery(id+"F4.imprint","IMPRINT",EDGE,{"disambiguationData":[TD([[subQ103,1.0]])],"derivedFrom":subQ98}),1.0]])]}),makeQuery(id+"F4.imprint","IMPRINT",FACE,{"disambiguationData":[TD([[makeQuery(id+"F4.imprint","IMPRINT",EDGE,{"disambiguationData":[TD([[subQ110,-1.0]])],"derivedFrom":subQ106}),1.0]])]}),makeQuery(id+"F4.imprint","IMPRINT",FACE,{"disambiguationData":[TD([[makeQuery(id+"F4.imprint","IMPRINT",EDGE,{"disambiguationData":[TD([[subQ110,1.0]])],"derivedFrom":subQ106}),1.0]])]}),makeQuery(id+"F4.imprint","IMPRINT",FACE,{"disambiguationData":[TD([[makeQuery(id+"F4.imprint","IMPRINT",EDGE,{"disambiguationData":[TD([[subQ116,1.0]])],"derivedFrom":subQ112}),1.0]])]}),makeQuery(id+"F4.imprint","IMPRINT",FACE,{"disambiguationData":[TD([[makeQuery(id+"F4.imprint","IMPRINT",EDGE,{"disambiguationData":[TD([[subQ116,-1.0]])],"derivedFrom":subQ112}),1.0]])]}),makeQuery(id+"F4.imprint","IMPRINT",FACE,{"disambiguationData":[TD([[makeQuery(id+"F4.imprint","IMPRINT",EDGE,{"disambiguationData":[TD([[subQ124,1.0]])],"derivedFrom":subQ119}),1.0]])]}),makeQuery(id+"F4.imprint","IMPRINT",FACE,{"disambiguationData":[TD([[makeQuery(id+"F4.imprint","IMPRINT",EDGE,{"disambiguationData":[TD([[subQ124,-1.0]])],"derivedFrom":subQ119}),1.0]])]}),makeQuery(id+"F4.imprint","IMPRINT",FACE,{"disambiguationData":[TD([[makeQuery(id+"F4.imprint","IMPRINT",EDGE,{"disambiguationData":[TD([[subQ131,-1.0]])],"derivedFrom":subQ126}),1.0]])]}),makeQuery(id+"F4.imprint","IMPRINT",FACE,{"disambiguationData":[TD([[makeQuery(id+"F4.imprint","IMPRINT",EDGE,{"disambiguationData":[TD([[subQ131,1.0]])],"derivedFrom":subQ126}),1.0]])]}),makeQuery(id+"F4.imprint","IMPRINT",FACE,{"disambiguationData":[TD([[makeQuery(id+"F4.imprint","IMPRINT",EDGE,{"disambiguationData":[TD([[subQ138,-1.0]])],"derivedFrom":subQ134}),1.0]])]}),makeQuery(id+"F4.imprint","IMPRINT",FACE,{"disambiguationData":[TD([[makeQuery(id+"F4.imprint","IMPRINT",EDGE,{"disambiguationData":[TD([[subQ138,1.0]])],"derivedFrom":subQ134}),1.0]])]}),makeQuery(id+"F4.imprint","IMPRINT",FACE,{"disambiguationData":[TD([[makeQuery(id+"F4.imprint","IMPRINT",EDGE,{"disambiguationData":[TD([[subQ144,-1.0]])],"derivedFrom":subQ140}),1.0]])]}),makeQuery(id+"F4.imprint","IMPRINT",FACE,{"disambiguationData":[TD([[makeQuery(id+"F4.imprint","IMPRINT",EDGE,{"disambiguationData":[TD([[subQ144,1.0]])],"derivedFrom":subQ140}),1.0]])]}),makeQuery(id+"F4.imprint","IMPRINT",FACE,{"disambiguationData":[TD([[makeQuery(id+"F4.imprint","IMPRINT",EDGE,{"disambiguationData":[TD([[subQ152,1.0]])],"derivedFrom":subQ147}),1.0]])]}),makeQuery(id+"F4.imprint","IMPRINT",FACE,{"disambiguationData":[TD([[makeQuery(id+"F4.imprint","IMPRINT",EDGE,{"disambiguationData":[TD([[subQ152,-1.0]])],"derivedFrom":subQ147}),1.0]])]}),makeQuery(id+"F4.imprint","IMPRINT",FACE,{"disambiguationData":[TD([[makeQuery(id+"F4.imprint","IMPRINT",EDGE,{"disambiguationData":[TD([[subQ159,-1.0]])],"derivedFrom":subQ154}),1.0]])]}),makeQuery(id+"F4.imprint","IMPRINT",FACE,{"disambiguationData":[TD([[makeQuery(id+"F4.imprint","IMPRINT",EDGE,{"disambiguationData":[TD([[subQ159,1.0]])],"derivedFrom":subQ154}),1.0]])]}),makeQuery(id+"F4.imprint","IMPRINT",FACE,{"disambiguationData":[TD([[makeQuery(id+"F4.imprint","IMPRINT",EDGE,{"disambiguationData":[TD([[subQ166,-1.0]])],"derivedFrom":subQ162}),1.0]])]}),makeQuery(id+"F4.imprint","IMPRINT",FACE,{"disambiguationData":[TD([[makeQuery(id+"F4.imprint","IMPRINT",EDGE,{"disambiguationData":[TD([[subQ166,1.0]])],"derivedFrom":subQ162}),1.0]])]}),makeQuery(id+"F4.imprint","IMPRINT",FACE,{"disambiguationData":[TD([[makeQuery(id+"F4.imprint","IMPRINT",EDGE,{"disambiguationData":[TD([[subQ172,-1.0]])],"derivedFrom":subQ168}),1.0]])]}),makeQuery(id+"F4.imprint","IMPRINT",FACE,{"disambiguationData":[TD([[makeQuery(id+"F4.imprint","IMPRINT",EDGE,{"disambiguationData":[TD([[subQ172,1.0]])],"derivedFrom":subQ168}),1.0]])]}),makeQuery(id+"F4.imprint","IMPRINT",FACE,{"disambiguationData":[TD([[makeQuery(id+"F4.imprint","IMPRINT",EDGE,{"disambiguationData":[TD([[subQ180,-1.0]])],"derivedFrom":subQ175}),1.0]])]}),makeQuery(id+"F4.imprint","IMPRINT",FACE,{"disambiguationData":[TD([[makeQuery(id+"F4.imprint","IMPRINT",EDGE,{"disambiguationData":[TD([[subQ180,1.0]])],"derivedFrom":subQ175}),1.0]])]}),makeQuery(id+"F4.imprint","IMPRINT",FACE,{"disambiguationData":[TD([[makeQuery(id+"F4.imprint","IMPRINT",EDGE,{"disambiguationData":[TD([[subQ187,-1.0]])],"derivedFrom":subQ182}),1.0]])]}),makeQuery(id+"F4.imprint","IMPRINT",FACE,{"disambiguationData":[TD([[makeQuery(id+"F4.imprint","IMPRINT",EDGE,{"disambiguationData":[TD([[subQ187,1.0]])],"derivedFrom":subQ182}),1.0]])]}),makeQuery(id+"F4.imprint","IMPRINT",FACE,{"disambiguationData":[TD([[makeQuery(id+"F4.imprint","IMPRINT",EDGE,{"disambiguationData":[TD([[subQ194,-1.0]])],"derivedFrom":subQ190}),1.0]])]}),makeQuery(id+"F4.imprint","IMPRINT",FACE,{"disambiguationData":[TD([[makeQuery(id+"F4.imprint","IMPRINT",EDGE,{"disambiguationData":[TD([[subQ194,1.0]])],"derivedFrom":subQ190}),1.0]])]}),makeQuery(id+"F4.imprint","IMPRINT",FACE,{"disambiguationData":[TD([[makeQuery(id+"F4.imprint","IMPRINT",EDGE,{"disambiguationData":[TD([[subQ200,1.0]])],"derivedFrom":subQ196}),1.0]])]}),makeQuery(id+"F4.imprint","IMPRINT",FACE,{"disambiguationData":[TD([[makeQuery(id+"F4.imprint","IMPRINT",EDGE,{"disambiguationData":[TD([[subQ200,-1.0]])],"derivedFrom":subQ196}),1.0]])]}),makeQuery(id+"F4.imprint","IMPRINT",FACE,{"disambiguationData":[TD([[makeQuery(id+"F4.imprint","IMPRINT",EDGE,{"disambiguationData":[TD([[subQ208,-1.0]])],"derivedFrom":subQ203}),1.0]])]}),makeQuery(id+"F4.imprint","IMPRINT",FACE,{"disambiguationData":[TD([[makeQuery(id+"F4.imprint","IMPRINT",EDGE,{"disambiguationData":[TD([[subQ208,1.0]])],"derivedFrom":subQ203}),1.0]])]}),makeQuery(id+"F4.imprint","IMPRINT",FACE,{"disambiguationData":[TD([[makeQuery(id+"F4.imprint","IMPRINT",EDGE,{"disambiguationData":[TD([[subQ215,-1.0]])],"derivedFrom":subQ210}),1.0]])]}),makeQuery(id+"F4.imprint","IMPRINT",FACE,{"disambiguationData":[TD([[makeQuery(id+"F4.imprint","IMPRINT",EDGE,{"disambiguationData":[TD([[subQ215,1.0]])],"derivedFrom":subQ210}),1.0]])]}),makeQuery(id+"F4.imprint","IMPRINT",FACE,{"disambiguationData":[TD([[makeQuery(id+"F4.imprint","IMPRINT",EDGE,{"disambiguationData":[TD([[subQ222,-1.0]])],"derivedFrom":subQ218}),1.0]])]}),makeQuery(id+"F4.imprint","IMPRINT",FACE,{"disambiguationData":[TD([[makeQuery(id+"F4.imprint","IMPRINT",EDGE,{"disambiguationData":[TD([[subQ222,1.0]])],"derivedFrom":subQ218}),1.0]])]}),makeQuery(id+"F4.imprint","IMPRINT",FACE,{"disambiguationData":[TD([[makeQuery(id+"F4.imprint","IMPRINT",EDGE,{"disambiguationData":[TD([[subQ228,1.0]])],"derivedFrom":subQ224}),1.0]])]}),makeQuery(id+"F4.imprint","IMPRINT",FACE,{"disambiguationData":[TD([[makeQuery(id+"F4.imprint","IMPRINT",EDGE,{"disambiguationData":[TD([[subQ228,-1.0]])],"derivedFrom":subQ224}),1.0]])]}),makeQuery(id+"F4.imprint","IMPRINT",FACE,{"disambiguationData":[TD([[makeQuery(id+"F4.imprint","IMPRINT",EDGE,{"disambiguationData":[TD([[subQ236,-1.0]])],"derivedFrom":subQ231}),1.0]])]}),makeQuery(id+"F4.imprint","IMPRINT",FACE,{"disambiguationData":[TD([[makeQuery(id+"F4.imprint","IMPRINT",EDGE,{"disambiguationData":[TD([[subQ236,1.0]])],"derivedFrom":subQ231}),1.0]])]}),makeQuery(id+"F4.imprint","IMPRINT",FACE,{"disambiguationData":[TD([[makeQuery(id+"F4.imprint","IMPRINT",EDGE,{"disambiguationData":[TD([[subQ243,-1.0]])],"derivedFrom":subQ238}),1.0]])]}),makeQuery(id+"F4.imprint","IMPRINT",FACE,{"disambiguationData":[TD([[makeQuery(id+"F4.imprint","IMPRINT",EDGE,{"disambiguationData":[TD([[subQ243,1.0]])],"derivedFrom":subQ238}),1.0]])]}),makeQuery(id+"F4.imprint","IMPRINT",FACE,{"disambiguationData":[TD([[makeQuery(id+"F4.imprint","IMPRINT",EDGE,{"disambiguationData":[TD([[subQ250,-1.0]])],"derivedFrom":subQ246}),1.0]])]}),makeQuery(id+"F4.imprint","IMPRINT",FACE,{"disambiguationData":[TD([[makeQuery(id+"F4.imprint","IMPRINT",EDGE,{"disambiguationData":[TD([[subQ250,1.0]])],"derivedFrom":subQ246}),1.0]])]}),makeQuery(id+"F4.imprint","IMPRINT",FACE,{"disambiguationData":[TD([[makeQuery(id+"F4.imprint","IMPRINT",EDGE,{"disambiguationData":[TD([[subQ256,1.0]])],"derivedFrom":subQ252}),1.0]])]}),makeQuery(id+"F4.imprint","IMPRINT",FACE,{"disambiguationData":[TD([[makeQuery(id+"F4.imprint","IMPRINT",EDGE,{"disambiguationData":[TD([[subQ256,-1.0]])],"derivedFrom":subQ252}),1.0]])]}),makeQuery(id+"F4.imprint","IMPRINT",FACE,{"disambiguationData":[TD([[makeQuery(id+"F4.imprint","IMPRINT",EDGE,{"disambiguationData":[TD([[subQ264,-1.0]])],"derivedFrom":subQ259}),1.0]])]}),makeQuery(id+"F4.imprint","IMPRINT",FACE,{"disambiguationData":[TD([[makeQuery(id+"F4.imprint","IMPRINT",EDGE,{"disambiguationData":[TD([[subQ264,1.0]])],"derivedFrom":subQ259}),1.0]])]}),makeQuery(id+"F4.imprint","IMPRINT",FACE,{"disambiguationData":[TD([[makeQuery(id+"F4.imprint","IMPRINT",EDGE,{"disambiguationData":[TD([[subQ271,-1.0]])],"derivedFrom":subQ267}),1.0]])]}),makeQuery(id+"F4.imprint","IMPRINT",FACE,{"disambiguationData":[TD([[makeQuery(id+"F4.imprint","IMPRINT",EDGE,{"disambiguationData":[TD([[subQ271,1.0]])],"derivedFrom":subQ267}),1.0]])]}),makeQuery(id+"F4.imprint","IMPRINT",FACE,{"disambiguationData":[TD([[makeQuery(id+"F4.imprint","IMPRINT",EDGE,{"disambiguationData":[TD([[subQ278,-1.0]])],"derivedFrom":subQ273}),1.0]])]}),makeQuery(id+"F4.imprint","IMPRINT",FACE,{"disambiguationData":[TD([[makeQuery(id+"F4.imprint","IMPRINT",EDGE,{"disambiguationData":[TD([[subQ278,1.0]])],"derivedFrom":subQ273}),1.0]])]}),makeQuery(id+"F4.imprint","IMPRINT",FACE,{"disambiguationData":[TD([[makeQuery(id+"F4.imprint","IMPRINT",EDGE,{"disambiguationData":[TD([[subQ286,-1.0]])],"derivedFrom":subQ281}),1.0]])]}),makeQuery(id+"F4.imprint","IMPRINT",FACE,{"disambiguationData":[TD([[makeQuery(id+"F4.imprint","IMPRINT",EDGE,{"disambiguationData":[TD([[subQ286,1.0]])],"derivedFrom":subQ281}),1.0]])]}),makeQuery(id+"F4.imprint","IMPRINT",FACE,{"disambiguationData":[TD([[makeQuery(id+"F4.imprint","IMPRINT",EDGE,{"disambiguationData":[TD([[subQ293,-1.0]])],"derivedFrom":subQ288}),1.0]])]}),makeQuery(id+"F4.imprint","IMPRINT",FACE,{"disambiguationData":[TD([[makeQuery(id+"F4.imprint","IMPRINT",EDGE,{"disambiguationData":[TD([[subQ293,1.0]])],"derivedFrom":subQ288}),1.0]])]}),makeQuery(id+"F4.imprint","IMPRINT",FACE,{"disambiguationData":[TD([[makeQuery(id+"F4.imprint","IMPRINT",EDGE,{"disambiguationData":[TD([[subQ300,-1.0]])],"derivedFrom":subQ296}),1.0]])]}),makeQuery(id+"F4.imprint","IMPRINT",FACE,{"disambiguationData":[TD([[makeQuery(id+"F4.imprint","IMPRINT",EDGE,{"disambiguationData":[TD([[subQ300,1.0]])],"derivedFrom":subQ296}),1.0]])]}),makeQuery(id+"F4.imprint","IMPRINT",FACE,{"disambiguationData":[TD([[makeQuery(id+"F4.imprint","IMPRINT",EDGE,{"disambiguationData":[TD([[subQ306,1.0]])],"derivedFrom":subQ302}),1.0]])]}),makeQuery(id+"F4.imprint","IMPRINT",FACE,{"disambiguationData":[TD([[makeQuery(id+"F4.imprint","IMPRINT",EDGE,{"disambiguationData":[TD([[subQ306,-1.0]])],"derivedFrom":subQ302}),1.0]])]}),makeQuery(id+"F4.imprint","IMPRINT",FACE,{"disambiguationData":[TD([[makeQuery(id+"F4.imprint","IMPRINT",EDGE,{"disambiguationData":[TD([[subQ314,1.0]])],"derivedFrom":subQ309}),1.0]])]}),makeQuery(id+"F4.imprint","IMPRINT",FACE,{"disambiguationData":[TD([[makeQuery(id+"F4.imprint","IMPRINT",EDGE,{"disambiguationData":[TD([[subQ314,-1.0]])],"derivedFrom":subQ309}),1.0]])]}),makeQuery(id+"F4.imprint","IMPRINT",FACE,{"disambiguationData":[TD([[makeQuery(id+"F4.imprint","IMPRINT",EDGE,{"disambiguationData":[TD([[subQ321,-1.0]])],"derivedFrom":subQ317}),1.0]])]}),makeQuery(id+"F4.imprint","IMPRINT",FACE,{"disambiguationData":[TD([[makeQuery(id+"F4.imprint","IMPRINT",EDGE,{"disambiguationData":[TD([[subQ321,1.0]])],"derivedFrom":subQ317}),1.0]])]}),makeQuery(id+"F4.imprint","IMPRINT",FACE,{"disambiguationData":[TD([[makeQuery(id+"F4.imprint","IMPRINT",EDGE,{"disambiguationData":[TD([[subQ328,-1.0]])],"derivedFrom":subQ323}),1.0]])]}),makeQuery(id+"F4.imprint","IMPRINT",FACE,{"disambiguationData":[TD([[makeQuery(id+"F4.imprint","IMPRINT",EDGE,{"disambiguationData":[TD([[subQ328,1.0]])],"derivedFrom":subQ323}),1.0]])]}),makeQuery(id+"F4.imprint","IMPRINT",FACE,{"disambiguationData":[TD([[makeQuery(id+"F4.imprint","IMPRINT",EDGE,{"disambiguationData":[TD([[subQ334,-1.0]])],"derivedFrom":subQ330}),1.0]])]}),makeQuery(id+"F4.imprint","IMPRINT",FACE,{"disambiguationData":[TD([[makeQuery(id+"F4.imprint","IMPRINT",EDGE,{"disambiguationData":[TD([[subQ334,1.0]])],"derivedFrom":subQ330}),1.0]])]}),makeQuery(id+"F4.imprint","IMPRINT",FACE,{"disambiguationData":[TD([[makeQuery(id+"F4.imprint","IMPRINT",EDGE,{"disambiguationData":[TD([[subQ6,1.0]])],"derivedFrom":subQ1}),1.0]])]}),makeQuery(id+"F4.imprint","IMPRINT",FACE,{"disambiguationData":[TD([[makeQuery(id+"F4.imprint","IMPRINT",EDGE,{"disambiguationData":[TD([[subQ13,-1.0]])],"derivedFrom":subQ9}),1.0]])]}),makeQuery(id+"F4.imprint","IMPRINT",FACE,{"disambiguationData":[TD([[makeQuery(id+"F4.imprint","IMPRINT",EDGE,{"disambiguationData":[TD([[subQ21,1.0]])],"derivedFrom":subQ16}),1.0]])]}),makeQuery(id+"F4.imprint","IMPRINT",FACE,{"disambiguationData":[TD([[makeQuery(id+"F4.imprint","IMPRINT",EDGE,{"disambiguationData":[TD([[subQ29,-1.0]])],"derivedFrom":subQ24}),1.0]])]}),makeQuery(id+"F4.imprint","IMPRINT",FACE,{"disambiguationData":[TD([[makeQuery(id+"F4.imprint","IMPRINT",EDGE,{"disambiguationData":[TD([[subQ37,-1.0]])],"derivedFrom":subQ32}),1.0]])]}),makeQuery(id+"F4.imprint","IMPRINT",FACE,{"disambiguationData":[TD([[makeQuery(id+"F4.imprint","IMPRINT",EDGE,{"disambiguationData":[TD([[subQ45,1.0]])],"derivedFrom":subQ40}),1.0]])]}),makeQuery(id+"F4.imprint","IMPRINT",FACE,{"disambiguationData":[TD([[makeQuery(id+"F4.imprint","IMPRINT",EDGE,{"disambiguationData":[TD([[subQ52,-1.0]])],"derivedFrom":subQ48}),1.0]])]}),makeQuery(id+"F4.imprint","IMPRINT",FACE,{"disambiguationData":[TD([[makeQuery(id+"F4.imprint","IMPRINT",EDGE,{"disambiguationData":[TD([[subQ60,1.0]])],"derivedFrom":subQ55}),1.0]])]}),makeQuery(id+"F4.imprint","IMPRINT",FACE,{"disambiguationData":[TD([[makeQuery(id+"F4.imprint","IMPRINT",EDGE,{"disambiguationData":[TD([[subQ340,1.0]])],"derivedFrom":subQ336}),1.0]])]}),makeQuery(id+"F4.imprint","IMPRINT",FACE,{"disambiguationData":[TD([[makeQuery(id+"F4.imprint","IMPRINT",EDGE,{"disambiguationData":[TD([[subQ340,-1.0]])],"derivedFrom":subQ336}),1.0]])]})]);}
            extrude(context, id + "F5", {"entities" : qUnion([Q0]), "operationType" : NewBodyOperationType.REMOVE, "oppositeDirection" : true, "depth" : 25 * mm});
        }
    });
